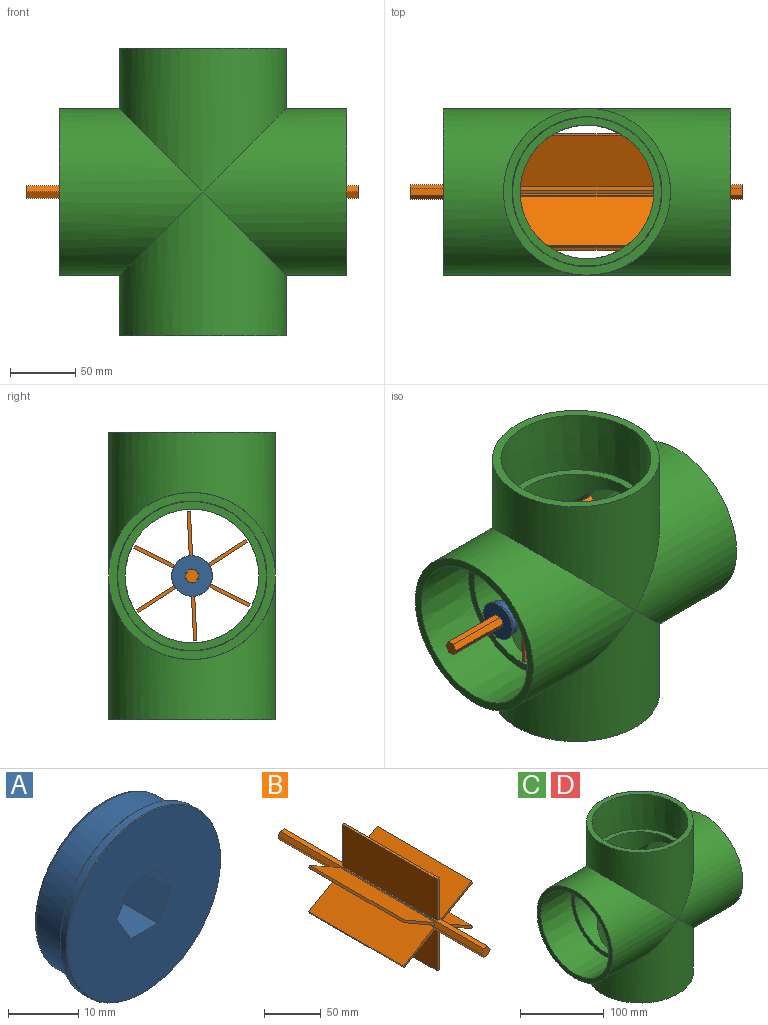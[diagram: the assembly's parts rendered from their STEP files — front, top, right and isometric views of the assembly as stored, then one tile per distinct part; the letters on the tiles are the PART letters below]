
ASSEMBLY  parts=4 mates=2
PART A: 17 faces, bbox 31.1x7.9x31.1 mm
  f0: torus R=13.78mm, axis (0,1,0), area 35.4mm2, adj f4,f13,f14
  f1: cone r=15.56mm half-angle=45deg, axis (0,1,0), area 17.5mm2, adj f2,f6
  f2: cylinder r=15.56mm len=31.12mm, axis (0,-1,0), area 124.1mm2, adj f1,f3
  f3: cone r=15.56mm half-angle=45deg, axis (0,-1,0), area 17.5mm2, adj f2,f15
  f4: cylinder r=14.29mm len=28.58mm, axis (0,-1,0), area 483.6mm2, adj f0,f14,f16
  f5: cylinder r=13.97mm len=27.94mm, axis (0,1,0), area 44.6mm2, adj f15,f16
  f6: plane 30.86x30.86mm, normal (0,-1,0), area 669.4mm2, adj f1,f7,f8,f9,f10,f11,f12
  f7: plane 7.93x4.76mm, normal (0.87,0,0.5), area 43.6mm2, adj f6,f8,f12,f13
  f8: plane 7.93x4.76mm, normal (0.87,0,-0.5), area 43.6mm2, adj f6,f7,f9,f13
  f9: plane 7.93x5.5mm, normal (0,0,-1), area 43.6mm2, adj f6,f8,f10,f13
  f10: plane 7.93x4.76mm, normal (-0.87,0,-0.5), area 43.6mm2, adj f6,f9,f11,f13
  f11: plane 7.93x4.76mm, normal (-0.87,0,0.5), area 43.6mm2, adj f6,f10,f12,f13
  f12: plane 7.93x5.5mm, normal (0,0,1), area 43.6mm2, adj f6,f7,f11,f13
  f13: plane 27.56x27.56mm, normal (0,1,0), area 517.9mm2, adj f0,f7,f8,f9,f10,f11,f12,f14
  f14: torus R=13.78mm, axis (0,1,0), area 35.4mm2, adj f0,f4,f13
  f15: plane 30.86x30.86mm, normal (0,1,0), area 134.9mm2, adj f3,f5
  f16: plane 28.58x28.58mm, normal (0,-1,0), area 28.2mm2, adj f4,f5
PART B: 38 faces, bbox 87.1x254x99.1 mm
  f0: plane 254x5.5mm, normal (0.01,0,-1), area 1096.2mm2, adj f1,f5,f6,f7,f33,f34,f35,f36
  f1: plane 254x4.79mm, normal (0.87,0,-0.49), area 1096.2mm2, adj f0,f2,f6,f7,f29,f30,f31,f32
  f2: plane 254x4.73mm, normal (0.86,0,0.51), area 1096.2mm2, adj f1,f3,f6,f7,f24,f25,f26,f27
  f3: plane 254x5.5mm, normal (-0.01,0,1), area 1096.2mm2, adj f2,f4,f6,f7,f19,f20,f21,f22
  f4: plane 254x4.79mm, normal (-0.87,0,0.49), area 1096.2mm2, adj f3,f5,f6,f7,f14,f15,f16,f17
  f5: plane 254x4.73mm, normal (-0.86,0,-0.51), area 1096.2mm2, adj f0,f4,f6,f7,f9,f10,f11,f12
  f6: plane 11x9.58mm, normal (0,-1,0), area 78.6mm2, adj f0,f1,f2,f3,f4,f5
  f7: plane 11x9.58mm, normal (0,1,0), area 78.6mm2, adj f0,f1,f2,f3,f4,f5
  f8: plane 118.36x2.2mm, normal (-0.87,0,-0.5), area 300.6mm2, adj f9,f10,f11,f12
  f9: plane 40.05x24.58mm, normal (0,1,0), area 113.7mm2, adj f5,f8,f11,f12
  f10: plane 40.05x24.58mm, normal (0,-1,0), area 113.7mm2, adj f5,f8,f11,f12
  f11: plane 118.36x38.78mm, normal (0.5,0,-0.87), area 5300.4mm2, adj f5,f8,f9,f10
  f12: plane 118.36x38.76mm, normal (-0.5,0,0.87), area 5297.2mm2, adj f5,f8,f9,f10
  f13: plane 118.36x2.2mm, normal (-0.87,0,0.5), area 300.6mm2, adj f14,f15,f16,f17
  f14: plane 40.03x24.59mm, normal (0,1,0), area 113.7mm2, adj f4,f13,f16,f17
  f15: plane 40.03x24.59mm, normal (0,-1,0), area 113.7mm2, adj f4,f13,f16,f17
  f16: plane 118.36x38.78mm, normal (-0.5,0,-0.87), area 5300.4mm2, adj f4,f13,f14,f15
  f17: plane 118.36x38.76mm, normal (0.5,0,0.87), area 5297.2mm2, adj f4,f13,f14,f15
  f18: plane 118.36x2.54mm, normal (0,0,1), area 300.6mm2, adj f19,f20,f21,f22
  f19: plane 44.78x2.54mm, normal (0,-1,0), area 113.7mm2, adj f3,f18,f21,f22
  f20: plane 44.78x2.54mm, normal (0,1,0), area 113.7mm2, adj f3,f18,f21,f22
  f21: plane 118.36x44.75mm, normal (1,0,0), area 5297.2mm2, adj f3,f18,f19,f20
  f22: plane 118.36x44.78mm, normal (-1,0,0), area 5300.4mm2, adj f3,f18,f19,f20
  f23: plane 118.36x2.2mm, normal (0.87,0,0.5), area 300.6mm2, adj f24,f25,f26,f27
  f24: plane 40.05x24.58mm, normal (0,-1,0), area 113.7mm2, adj f2,f23,f26,f27
  f25: plane 40.05x24.58mm, normal (0,1,0), area 113.7mm2, adj f2,f23,f26,f27
  f26: plane 118.36x38.78mm, normal (-0.5,0,0.87), area 5300.4mm2, adj f2,f23,f24,f25
  f27: plane 118.36x38.76mm, normal (0.5,0,-0.87), area 5297.2mm2, adj f2,f23,f24,f25
  f28: plane 118.36x2.2mm, normal (0.87,0,-0.5), area 300.6mm2, adj f29,f30,f31,f32
  f29: plane 40.03x24.59mm, normal (0,-1,0), area 113.7mm2, adj f1,f28,f31,f32
  f30: plane 40.03x24.59mm, normal (0,1,0), area 113.7mm2, adj f1,f28,f31,f32
  f31: plane 118.36x38.78mm, normal (0.5,0,0.87), area 5300.4mm2, adj f1,f28,f29,f30
  f32: plane 118.36x38.76mm, normal (-0.5,0,-0.87), area 5297.2mm2, adj f1,f28,f29,f30
  f33: plane 118.36x44.75mm, normal (-1,0,0), area 5297.2mm2, adj f0,f35,f36,f37
  f34: plane 118.36x44.78mm, normal (1,0,0), area 5300.4mm2, adj f0,f35,f36,f37
  f35: plane 44.78x2.54mm, normal (0,-1,0), area 113.7mm2, adj f0,f33,f34,f37
  f36: plane 44.78x2.54mm, normal (0,1,0), area 113.7mm2, adj f0,f33,f34,f37
  f37: plane 118.36x2.54mm, normal (0,0,-1), area 300.6mm2, adj f33,f34,f35,f36
PART C: 20 faces, bbox 220x127.8x220 mm
  f0: plane 114.07x114.07mm, normal (0,0,1), area 2006.8mm2, adj f10,f18
  f1: plane 114.07x114.07mm, normal (0,0,-1), area 2006.8mm2, adj f16,f19
  f2: cylinder r=51.13mm len=102.26mm, axis (1,0,0), area 8555.7mm2, adj f5,f18,f19
  f3: cylinder r=51.13mm len=102.26mm, axis (1,0,0), area 8555.7mm2, adj f4,f18,f19
  f4: plane 114.07x114.07mm, normal (-1,0,0), area 2006.8mm2, adj f3,f8
  f5: plane 114.07x114.07mm, normal (1,0,0), area 2006.8mm2, adj f2,f9
  f6: cylinder r=63.88mm len=127.76mm, axis (-1,0,0), area 27821mm2, adj f12,f14,f15
  f7: cylinder r=63.88mm len=127.76mm, axis (-1,0,0), area 27821mm2, adj f12,f13,f15
  f8: cone r=57.04mm half-angle=0.4deg, axis (-1,0,0), area 18260.1mm2, adj f4,f13
  f9: cone r=57.38mm half-angle=0.4deg, axis (1,0,0), area 18260.1mm2, adj f5,f14
  f10: cone r=57.38mm half-angle=0.4deg, axis (0,0,1), area 18260.1mm2, adj f0,f11
  f11: plane 127.76x127.76mm, normal (0,0,1), area 2477.1mm2, adj f10,f12
  f12: cylinder r=63.88mm len=127.76mm, axis (0,0,-1), area 27821mm2, adj f6,f7,f11
  f13: plane 127.76x127.76mm, normal (-1,0,0), area 2477.1mm2, adj f7,f8
  f14: plane 127.76x127.76mm, normal (1,0,0), area 2477.1mm2, adj f6,f9
  f15: cylinder r=63.88mm len=127.76mm, axis (0,0,1), area 27821mm2, adj f6,f7,f17
  f16: cone r=57.04mm half-angle=0.4deg, axis (0,0,-1), area 18260.1mm2, adj f1,f17
  f17: plane 127.76x127.76mm, normal (0,0,-1), area 2477.1mm2, adj f15,f16
  f18: cylinder r=51.13mm len=102.26mm, axis (0,0,1), area 8555.7mm2, adj f0,f2,f3
  f19: cylinder r=51.13mm len=102.26mm, axis (0,0,1), area 8555.7mm2, adj f1,f2,f3
PART D: same geometry as C
PLACE A rot(axis=(0.57,0.57,-0.6),118.3deg) t=(-76.65,0,0)mm
PLACE B rot(axis=(0.71,-0.71,0.02),177.9deg) t=(-135.38,0,0)mm
PLACE C at identity fixed
PLACE D at identity
MATE fastened B.f7 <-> A.f1  axis (-1,0,0) through (-135.38,0,0)mm
MATE revolute B.f7 <-> C.f2  axis (-1,0,0) through (-135.38,0,0)mm
